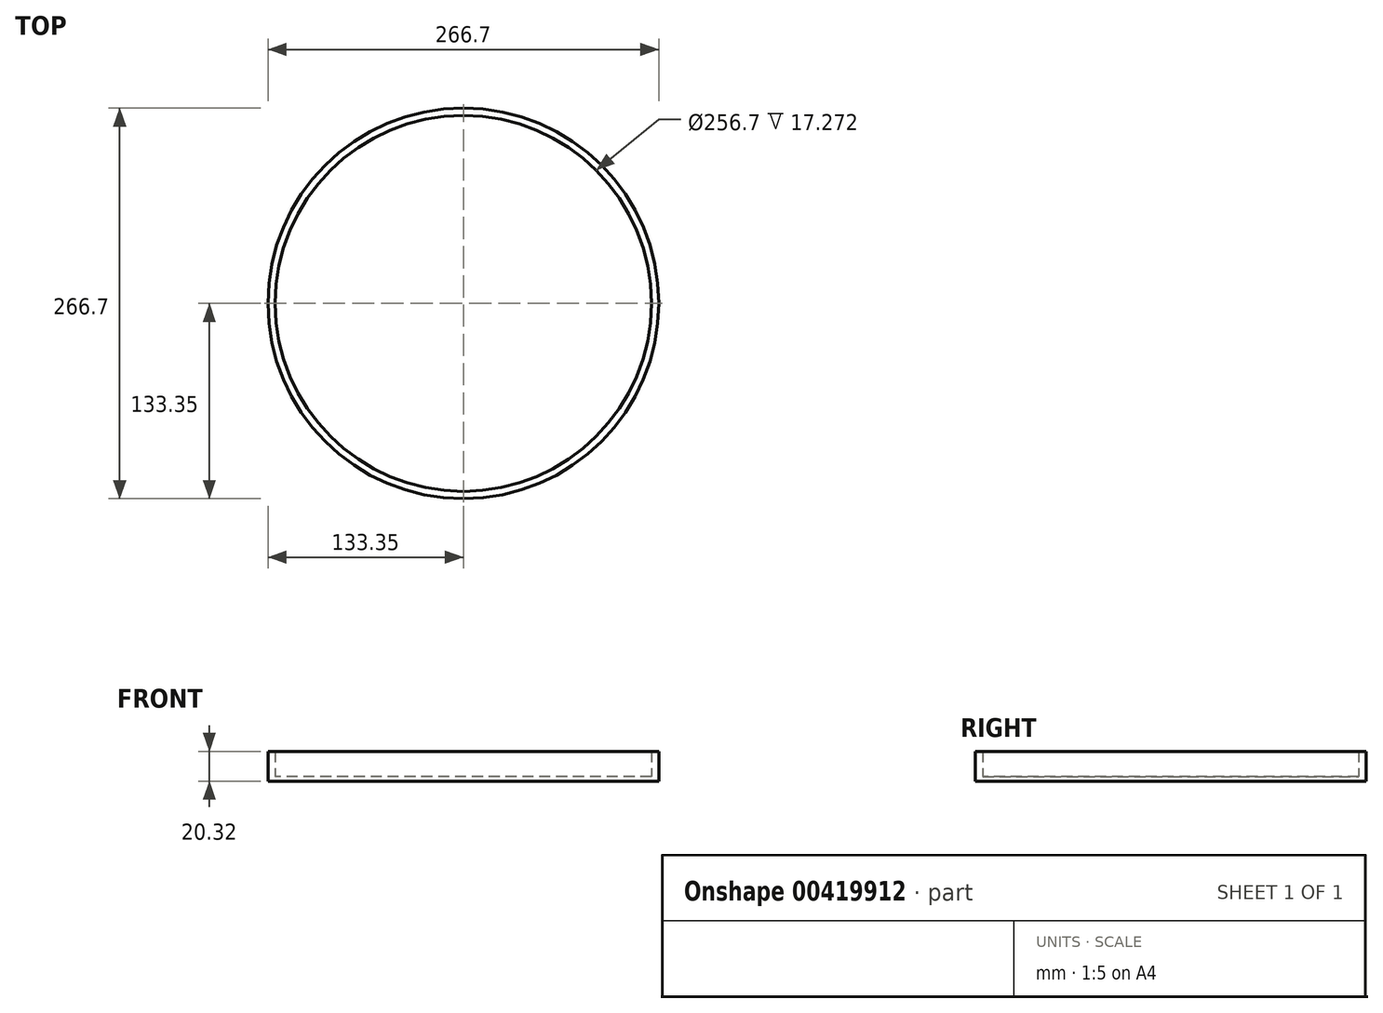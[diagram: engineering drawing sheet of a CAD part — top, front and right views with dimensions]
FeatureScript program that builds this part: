
annotation { "Feature Type Name" : "Feature", "Feature Type Description" : "" }
export const myFeature = defineFeature(function(context is Context, id is Id, definition is map)
    precondition{}
    {
        {
            var Q0;
            Q0=qCreatedBy(makeId("Top.planeOp"),FACE);
            var sketch = newSketch(context, id + "F0", { "sketchPlane" : qUnion([Q0])});
            skCircle(sketch, "E0", {"center": v(0, 0) * mm, "radius": 133.35 * mm});
            skSolve(sketch);
        }
        {
            var Q0;
            Q0 = qSketchRegion(id + "F0", true);
            var Q1;
            Q1 = qConstructionFilter(qBodyType(qCreatedBy(id + "F0" ,EDGE), BodyType.WIRE), ConstructionObject.NO);
            extrude(context, id + "F1", {"entities" : qUnion([Q0]), "surfaceEntities" : qUnion([Q1]), "depth" : 20.32 * mm});
        }
        {
            var Q0;
            Q0=makeQuery(id+"F1.opExtrude","CAP_FACE",FACE,{"disambiguationData":[OSD([sQuery(id+"F0.wireOp",EDGE,"E0")])],"isStart":false});
            var sketch = newSketch(context, id + "F2", { "sketchPlane" : qUnion([Q0])});
            skCircle(sketch, "E1.0", {"center": v(0, 0) * mm, "radius": 128.35 * mm});
            skSolve(sketch);
        }
        {
            var Q0;
            Q0 = qSketchRegion(id + "F2", true);
            var Q1;
            Q1=sQuery(id+"F2.wireOp",EDGE,"E1.0");
            extrude(context, id + "F3", {"entities" : qUnion([Q0]), "operationType" : NewBodyOperationType.REMOVE, "surfaceEntities" : qUnion([Q1]), "oppositeDirection" : true, "depth" : 17.27 * mm, "hasDraft" : true, "draftAngle" : 0 * degree, "draftPullDirection" : true});
        }
    });
